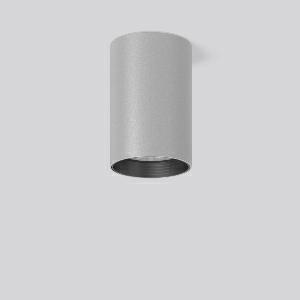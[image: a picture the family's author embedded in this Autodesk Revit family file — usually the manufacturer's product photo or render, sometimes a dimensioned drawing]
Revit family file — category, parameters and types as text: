
# Revit family: heledon_maxi_a_931241_004_5000
name_source: partatom
category: Lighting Fixtures
units: mm (PartAtom-declared; Revit-internal decimal feet)

## family parameters
Cut with Voids When Loaded = No
Host = Face
Light Source = No
Part Type = Normal
Room Calculation Point = No
Round Connector Dimension = Use Diameter
Shared = No

## types (1)
- HELEDON maxi A (1 x LED Modul 920 meat+, 1900 lm, 2000)
    Apparent Load = 33 VA
    Approval mark = CE
    CIE Flux Codes = 97 100 100 100 100
    Color Rendering = 90
    Color Temperature = 2000
    Default Elevation = 1800 mm
    Description = Series: HELEDON maxi
Cylindrical surface-mounted downlight. Housing: die-cast aluminium, powder-coated. Internal ceiling frame polycarbonate with bayonet mounting. Black plastic ring and recessed LED to prevent glare from the side. Optical assembly with lens made of plastic (polycarbonate) for the best homogeneous light distribution - can be changed without tools. Special LED for illumination of meat included. Suitable for Ceiling mounting. Easy installation with a separate ceiling frame with bayonet mounting and plug connection. Driver integrated. Connected via plug-in connector. High quality converter without flickering and stroboscopic effect. The following accessories can be mounted without use of tools: interchangeable lenses, decorative glasses, honeycomb louvre, clear and frosted diffusers, white interchangeable plastic ring. 
Colour: silver
Diameter: 123 mm
Height: 183 mm
Lamp: LED
Socket: without socket
Colour temperature: meat +
System power: 33 W
Rated luminous flux: 1900 lm
Luminous efficiency: 58 lm/W
Control gear: Regulated power supply
Protection class: I
Type of protection: IP 20
    Height = 183 mm
    Lamp = 1 x LED Modul 920 meat+
    Lamp Light Flux = 1900 lm
    Lamp count = 1
    Length = 123 mm
    Lifetime = 50000 h
    Luminous efficacy = 58 lm/W
    Manufacturer = RZB
    ModVariant = No
    Model = 931241.004
    Mounting Place = Ceiling
    Mounting Type = Surface mounted
    Number of Poles = 1
    OnlyDefault = Yes
    Power Factor = 1
    Product Name = HELEDON maxi A
    Product group = Surface mounted downlights
    ProductGroupID = 302
    Protection Class = Protection class I
    Protection Degree = IP 20
    RLX_Detail_Level = 1
    RLX_Emergency_Light_Flux = 0 lm
    RLX_Emergency_Type = 0
    RLX_Emergency_Type_DB = No
    RlxData = <blob elided: 96965 chars, md5=a068bda9>
    Socket = socket
    Standby Power = 0 W
    System Light Flux = 1900 lm
    System Power = 33 W
    Type Comments = Product without accessories
    Type Image = 931193.004.jpg
    URL = http://relux.com
    VarID = ---
    Voltage = 230 V
    Voltage Range = 220-240 V
    Weight = 0.00 kg
    Width = 0 mm  [stored 0 ft]

note: [stored X ft] marks values corroborated as IEEE doubles in the binary element streams (Revit-internal decimal feet)

## geometry (parser evidence)
native form markers: Blend x4, Sweep x8
no freeform markers — native parametric forms only
